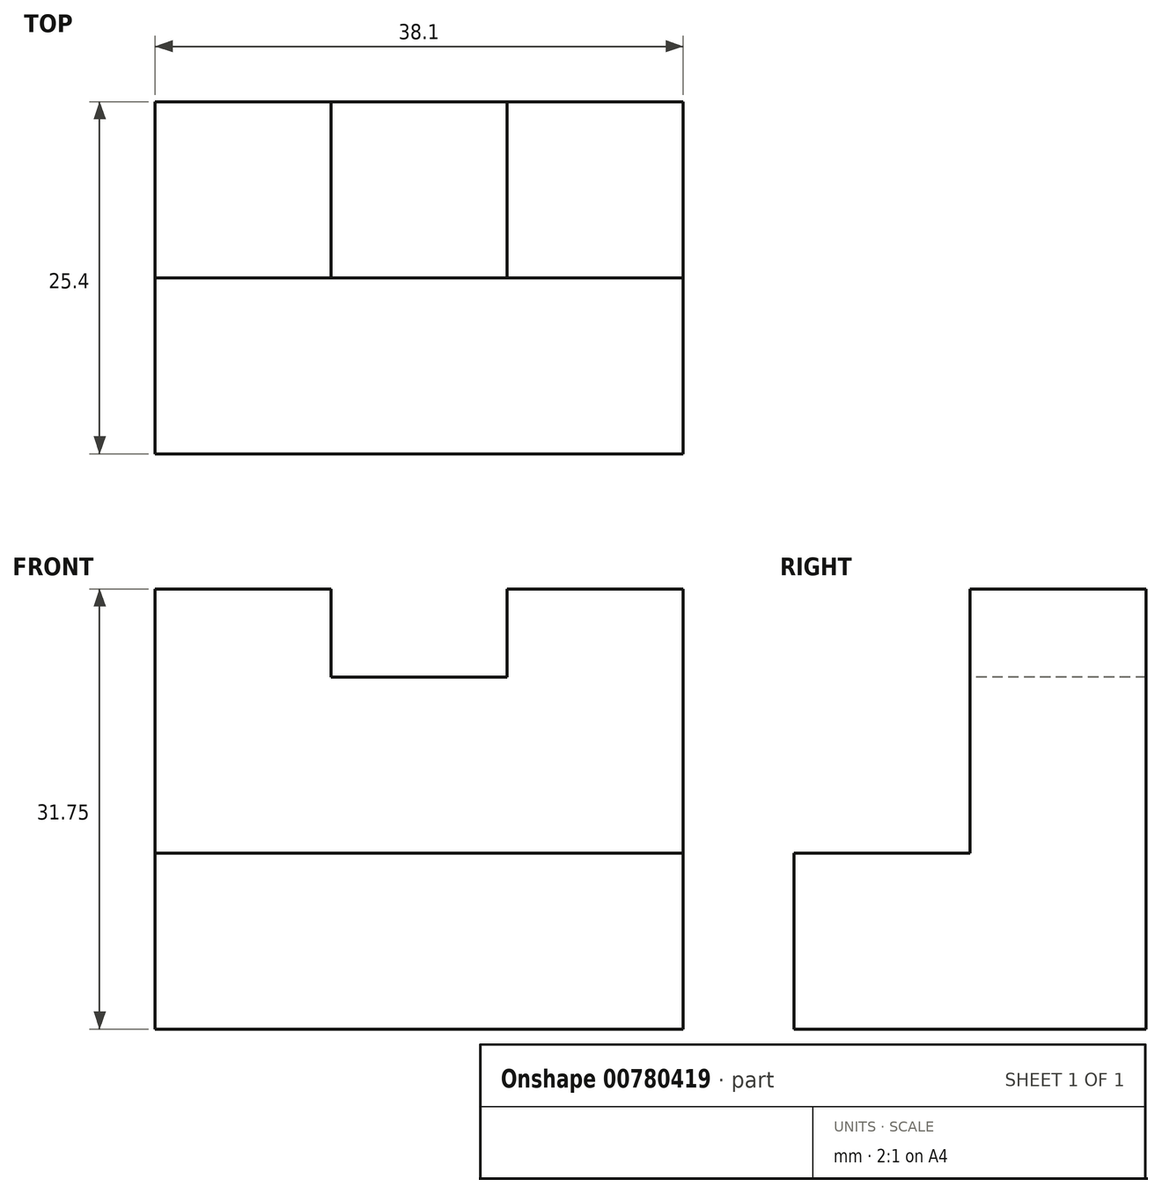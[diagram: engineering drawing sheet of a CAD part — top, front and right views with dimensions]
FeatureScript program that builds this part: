
annotation { "Feature Type Name" : "Feature", "Feature Type Description" : "" }
export const myFeature = defineFeature(function(context is Context, id is Id, definition is map)
    precondition{}
    {
        {
            var Q0;
            Q0=qCreatedBy(makeId("Front.planeOp"),FACE);
            var sketch = newSketch(context, id + "F0", { "sketchPlane" : qUnion([Q0])});
            skLineSegment(sketch, "E0", {"start": v(0, 0) * mm, "end": v(0, 12.7) * mm});
            skLineSegment(sketch, "E1", {"start": v(0, 12.7) * mm, "end": v(-38.1, 12.7) * mm});
            skLineSegment(sketch, "E2", {"start": v(-38.1, 12.7) * mm, "end": v(-38.1, 0) * mm});
            skLineSegment(sketch, "E3", {"start": v(-38.1, 0) * mm, "end": v(0, 0) * mm});
            skSolve(sketch);
        }
        {
            var Q0;
            Q0=makeQuery(id+"F0.imprint","IMPRINT",FACE,{"disambiguationData":[TD([[makeQuery(id+"F0.imprint","IMPRINT",EDGE,{"derivedFrom":sQuery(id+"F0.wireOp",EDGE,"E0")}),1.0]])]});
            extrude(context, id + "F1", {"entities" : qUnion([Q0]), "depth" : 12.7 * mm, "offsetDistance" : 25.4 * mm});
        }
        {
            var Q0;
            Q0=qCreatedBy(makeId("Right.planeOp"),FACE);
            var sketch = newSketch(context, id + "F2", { "sketchPlane" : qUnion([Q0])});
            skLineSegment(sketch, "E4", {"start": v(0, 0) * mm, "end": v(12.7, 0) * mm});
            skLineSegment(sketch, "E5", {"start": v(12.7, 0) * mm, "end": v(12.7, 31.75) * mm});
            skLineSegment(sketch, "E6", {"start": v(12.7, 31.75) * mm, "end": v(0, 31.75) * mm});
            skLineSegment(sketch, "E7", {"start": v(0, 31.75) * mm, "end": v(0, 0) * mm});
            skSolve(sketch);
        }
        {
            var Q0;
            Q0=makeQuery(id+"F2.imprint","IMPRINT",FACE,{"disambiguationData":[TD([[makeQuery(id+"F2.imprint","IMPRINT",EDGE,{"derivedFrom":sQuery(id+"F2.wireOp",EDGE,"E4")}),1.0]])]});
            extrude(context, id + "F3", {"entities" : qUnion([Q0]), "operationType" : NewBodyOperationType.ADD, "oppositeDirection" : true, "depth" : 38.1 * mm, "offsetDistance" : 25.4 * mm});
        }
        {
            var Q0;
            Q0=makeQuery(id+"F3.opExtrude","SWEPT_FACE",FACE,{"disambiguationData":[OSD([sQuery(id+"F2.wireOp",EDGE,"E7")])]});
            var sketch = newSketch(context, id + "F4", { "sketchPlane" : qUnion([Q0])});
            skLineSegment(sketch, "E8", {"start": v(-38.1, 31.75) * mm, "end": v(-25.4, 31.75) * mm});
            skLineSegment(sketch, "E9", {"start": v(-25.4, 31.75) * mm, "end": v(-25.4, 25.4) * mm});
            skLineSegment(sketch, "E10", {"start": v(-25.4, 25.4) * mm, "end": v(-12.7, 25.4) * mm});
            skLineSegment(sketch, "E11", {"start": v(-12.7, 25.4) * mm, "end": v(-12.7, 31.75) * mm});
            skLineSegment(sketch, "E12", {"start": v(-12.7, 31.75) * mm, "end": v(-25.4, 31.75) * mm});
            skSolve(sketch);
        }
        {
            var Q0;
            Q0=makeQuery(id+"F4.imprint","IMPRINT",FACE,{"disambiguationData":[TD([[makeQuery(id+"F4.imprint","IMPRINT",EDGE,{"derivedFrom":sQuery(id+"F4.wireOp",EDGE,"E9")}),1.0]])]});
            extrude(context, id + "F5", {"entities" : qUnion([Q0]), "operationType" : NewBodyOperationType.REMOVE, "oppositeDirection" : true, "depth" : 25.4 * mm, "offsetDistance" : 25.4 * mm});
        }
    });
